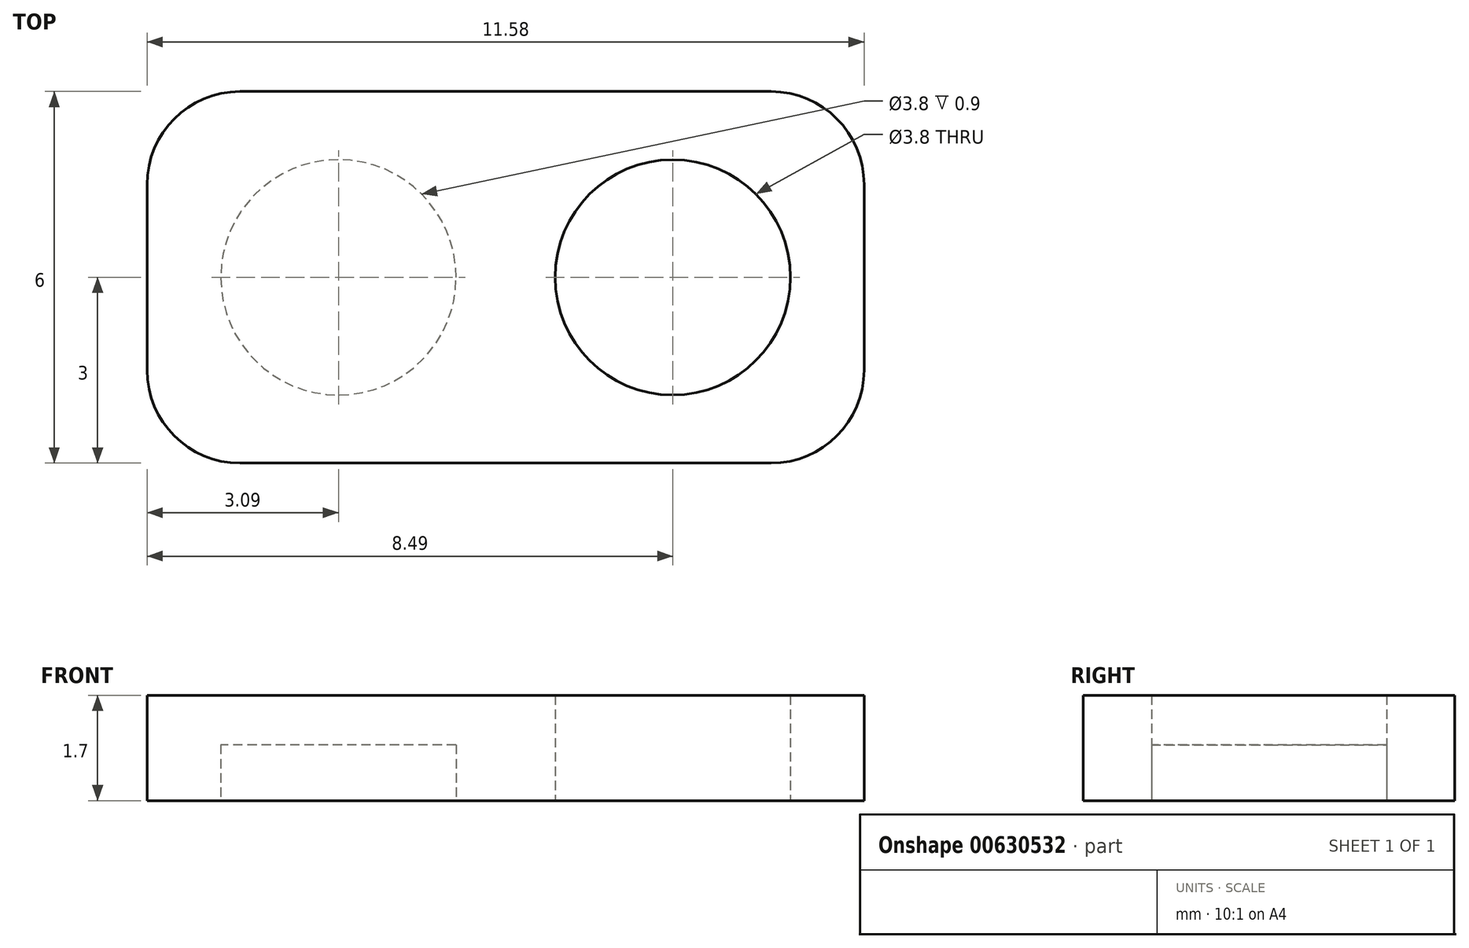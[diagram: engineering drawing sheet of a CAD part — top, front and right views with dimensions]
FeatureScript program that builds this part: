
annotation { "Feature Type Name" : "Feature", "Feature Type Description" : "" }
export const myFeature = defineFeature(function(context is Context, id is Id, definition is map)
    precondition{}
    {
        {
            var Q0;
            Q0=qCreatedBy(makeId("Top.planeOp"),FACE);
            var sketch = newSketch(context, id + "F0", { "sketchPlane" : qUnion([Q0])});
            skCircle(sketch, "E0", {"center": v(-2.7, 0) * mm, "radius": 1.9 * mm});
            skCircle(sketch, "E1.MirrorC", {"center": v(2.7, 0) * mm, "radius": 1.9 * mm});
            skLineSegment(sketch, "E2.bottom", {"start": v(-4.3, 3) * mm, "end": v(0.4, 3) * mm});
            skLineSegment(sketch, "E2.top", {"start": v(-4.3, -3) * mm, "end": v(0.4, -3) * mm});
            skLineSegment(sketch, "E2.left", {"start": v(-5.8, 1.5) * mm, "end": v(-5.8, -1.5) * mm});
            skLineSegment(sketch, "E3.MirrorCS", {"start": v(5.8, 1.5) * mm, "end": v(5.8, -1.5) * mm});
            skLineSegment(sketch, "E4.MirrorCS", {"start": v(4.3, -3) * mm, "end": v(-0.4, -3) * mm});
            skLineSegment(sketch, "E5.MirrorCS", {"start": v(4.3, 3) * mm, "end": v(-0.4, 3) * mm});
            skPoint(sketch, "E6.visualSharp", {"position": v(-5.8, -3) * mm});
            skArc(sketch, "E6.filletArc", {"start": v(-5.8, -1.5) * mm, "mid": v(-5.35, -2.56) * mm, "end": v(-4.3, -3) * mm});
            skPoint(sketch, "E7.visualSharp", {"position": v(-5.8, 3) * mm});
            skArc(sketch, "E7.filletArc", {"start": v(-4.3, 3) * mm, "mid": v(-5.35, 2.56) * mm, "end": v(-5.8, 1.5) * mm});
            skPoint(sketch, "E8.visualSharp", {"position": v(5.8, -3) * mm});
            skArc(sketch, "E8.filletArc", {"start": v(4.3, -3) * mm, "mid": v(5.35, -2.56) * mm, "end": v(5.8, -1.5) * mm});
            skPoint(sketch, "E9.visualSharp", {"position": v(5.8, 3) * mm});
            skArc(sketch, "E9.filletArc", {"start": v(5.8, 1.5) * mm, "mid": v(5.35, 2.56) * mm, "end": v(4.3, 3) * mm});
            skSolve(sketch);
        }
        {
            var Q0;
            Q0=makeQuery(id+"F0.imprint","IMPRINT",FACE,{"disambiguationData":[TD([[makeQuery(id+"F0.imprint","IMPRINT",EDGE,{"derivedFrom":sQuery(id+"F0.wireOp",EDGE,"E0")}),-1.0]])]});
            extrude(context, id + "F1", {"entities" : qUnion([Q0]), "depth" : 1.7 * mm, "offsetDistance" : 25 * mm});
        }
        {
            var Q0;
            Q0=makeQuery(id+"F1.opExtrude","CAP_FACE",FACE,{"disambiguationData":[OSD([sQuery(id+"F0.wireOp",EDGE,"E0"),sQuery(id+"F0.wireOp",EDGE,"E2.bottom"),sQuery(id+"F0.wireOp",EDGE,"E2.top"),sQuery(id+"F0.wireOp",EDGE,"E2.left"),sQuery(id+"F0.wireOp",EDGE,"E3.MirrorCS"),sQuery(id+"F0.wireOp",EDGE,"E4.MirrorCS"),sQuery(id+"F0.wireOp",EDGE,"E5.MirrorCS"),sQuery(id+"F0.wireOp",EDGE,"E1.MirrorC")])],"isStart":false});
            var sketch = newSketch(context, id + "F2", { "sketchPlane" : qUnion([Q0])});
            skLineSegment(sketch, "E10.0.0", {"start": v(-4.3, -3) * mm, "end": v(4.3, -3) * mm});
            skArc(sketch, "E10.0.1", {"start": v(4.3, -3) * mm, "mid": v(5.35, -2.56) * mm, "end": v(5.8, -1.5) * mm});
            skLineSegment(sketch, "E10.0.2", {"start": v(5.8, -1.5) * mm, "end": v(5.8, 1.5) * mm});
            skArc(sketch, "E10.0.3", {"start": v(5.8, 1.5) * mm, "mid": v(5.35, 2.56) * mm, "end": v(4.3, 3) * mm});
            skLineSegment(sketch, "E10.0.4", {"start": v(4.3, 3) * mm, "end": v(-4.3, 3) * mm});
            skArc(sketch, "E10.0.5", {"start": v(-4.3, 3) * mm, "mid": v(-5.35, 2.56) * mm, "end": v(-5.8, 1.5) * mm});
            skLineSegment(sketch, "E10.0.6", {"start": v(-5.8, 1.5) * mm, "end": v(-5.8, -1.5) * mm});
            skArc(sketch, "E10.0.7", {"start": v(-5.8, -1.5) * mm, "mid": v(-5.35, -2.56) * mm, "end": v(-4.3, -3) * mm});
            skSolve(sketch);
        }
        {
            var Q0;
            Q0=makeQuery(id+"F2.imprint","IMPRINT",FACE,{"disambiguationData":[TD([[makeQuery(id+"F2.imprint","IMPRINT",EDGE,{"derivedFrom":makeQuery(id+"F1.opExtrude","CAP_EDGE",EDGE,{"disambiguationData":[OSD([sQuery(id+"F0.wireOp",EDGE,"E0")])],"isStart":false})}),1.0]])]});
            var Q1;
            Q1=makeQuery(id+"F2.imprint","IMPRINT",FACE,{"disambiguationData":[TD([[makeQuery(id+"F2.imprint","IMPRINT",EDGE,{"derivedFrom":makeQuery(id+"F1.opExtrude","CAP_EDGE",EDGE,{"disambiguationData":[OSD([sQuery(id+"F0.wireOp",EDGE,"E1.MirrorC")])],"isStart":false})}),-1.0]])]});
            var Q2;
            Q2=makeQuery(id+"F2.imprint","IMPRINT",FACE,{"disambiguationData":[TD([[makeQuery(id+"F2.imprint","IMPRINT",EDGE,{"derivedFrom":sQuery(id+"F2.wireOp",EDGE,"3f5e1212-d70e-4376-afee-a36defe252fd.0.0")}),-1.0]])]});
            extrude(context, id + "F3", {"entities" : qUnion([Q0, Q1, Q2]), "operationType" : NewBodyOperationType.ADD, "oppositeDirection" : true, "depth" : .8 * mm, "offsetDistance" : 25 * mm});
        }
    });
